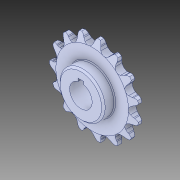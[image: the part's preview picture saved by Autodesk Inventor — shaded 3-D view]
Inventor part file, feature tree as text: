
AUTODESK INVENTOR PART (.ipt)
format: ipt  version: 2019 (Build 230136000, 136)  size: 466,944 bytes
history: native  units: in
note: dims shown in document units (in); Inventor stores cm internally (conversion verified against a paired STEP export)
features: chamfer x1
ambient origin geometry x8: Origin, YZ Plane, XZ Plane, XY Plane, X Axis, Y Axis, Z Axis, Center Point
bodies: Solid1 (feature_tree)
feature tree (1):
  chamfer  "Chamfer1"  [1 undecoded]
note: 1 required parameter value undecoded (feature->parameter linkage not recoverable at this tier; creation-order binding heuristic only, values carry confidence <= 0.55)
